# Revit family: EDLR-410-xxx-DPSx
name_source: partatom
category: Leuchten
units: mm (PartAtom-declared; Revit-internal decimal feet)

## family parameters
Basisbauteil = Fläche
Beim Laden mit Abzugskörper schneiden = Ja
Bemaßung runder Anschluss = Durchmesser verwenden
Gemeinsam genutzt = Nein
Lichtquelle = Ja
OmniClass-Nummer = 23.80.70.11
OmniClass-Titel = Luminaries for Internal Lighting
Raumberechnungspunkt = Nein
Teiletyp = Normal

## types (9) — shared parameters
Baugruppenkennzeichen = D5020200
Datei für fotometrisches Netz = EDLR 410_6000840 DPS.IES
Emissionsform beim Rendern sichtbar = Nein
Farbfilter = 16777215
Farbtemperaturverschiebung bei Dämpfen der Lampe = <Keine Auswahl>
Hersteller = RIDI Leuchten GmbH
Lampe = LED
Neigungswinkel = 90.00°
URL = www.ridi.de
Von Kreisdurchmesser aussenden = 300 mm
brand = RIDI
conformity mark = CE
electrical safety class = 1
height = 85 mm  [stored 0.278871 ft]
ingress protection (IP) code = IP20
length = 410 mm  [stored 1.34514 ft]
nominal frequency = 50-60Hz
nominal voltage = 230
voltage type (AC, DC, UC) = AC
weight = 2.6 kg
width = 410 mm  [stored 1.34514 ft]
zero-valued in all types: Vorgabe-Ansicht

## per-type parameters (varying)
| type | Modell | Scheinlast | rated input power |
| EDLR 410/5000-840 DPS | 0320250 | 30 VA | 30 |
| EDLR 410/5000-840 DPS-DALI | 0330250 | 30 VA | 30 |
| EDLR 410/6000-840 DPS | 0321212 | 37 VA | 37 |
| EDLR 410/6000-840 DPS-DALI | 0331212 | 37 VA | 37 |
| EDLR 410/5000-830 DPS | 0326713 | 30 VA | 30 |
| EDLR 410/5000-830 DPS-DALI | 0336713 | 30 VA | 30 |
| EDLR 410/6000-830 DPS | 0326717 | 37 VA | 37 |
| EDLR 410/6000-830 DPS-DALI | 0336717 | 37 VA | 37 |
| EDLR 410/6000-8TW DPS-DALI | 0336778 | 37 VA | 37 |

note: column(s) folded — value = type name in every type: product name

note: [stored X ft] marks values corroborated as IEEE doubles in the binary element streams (Revit-internal decimal feet)
